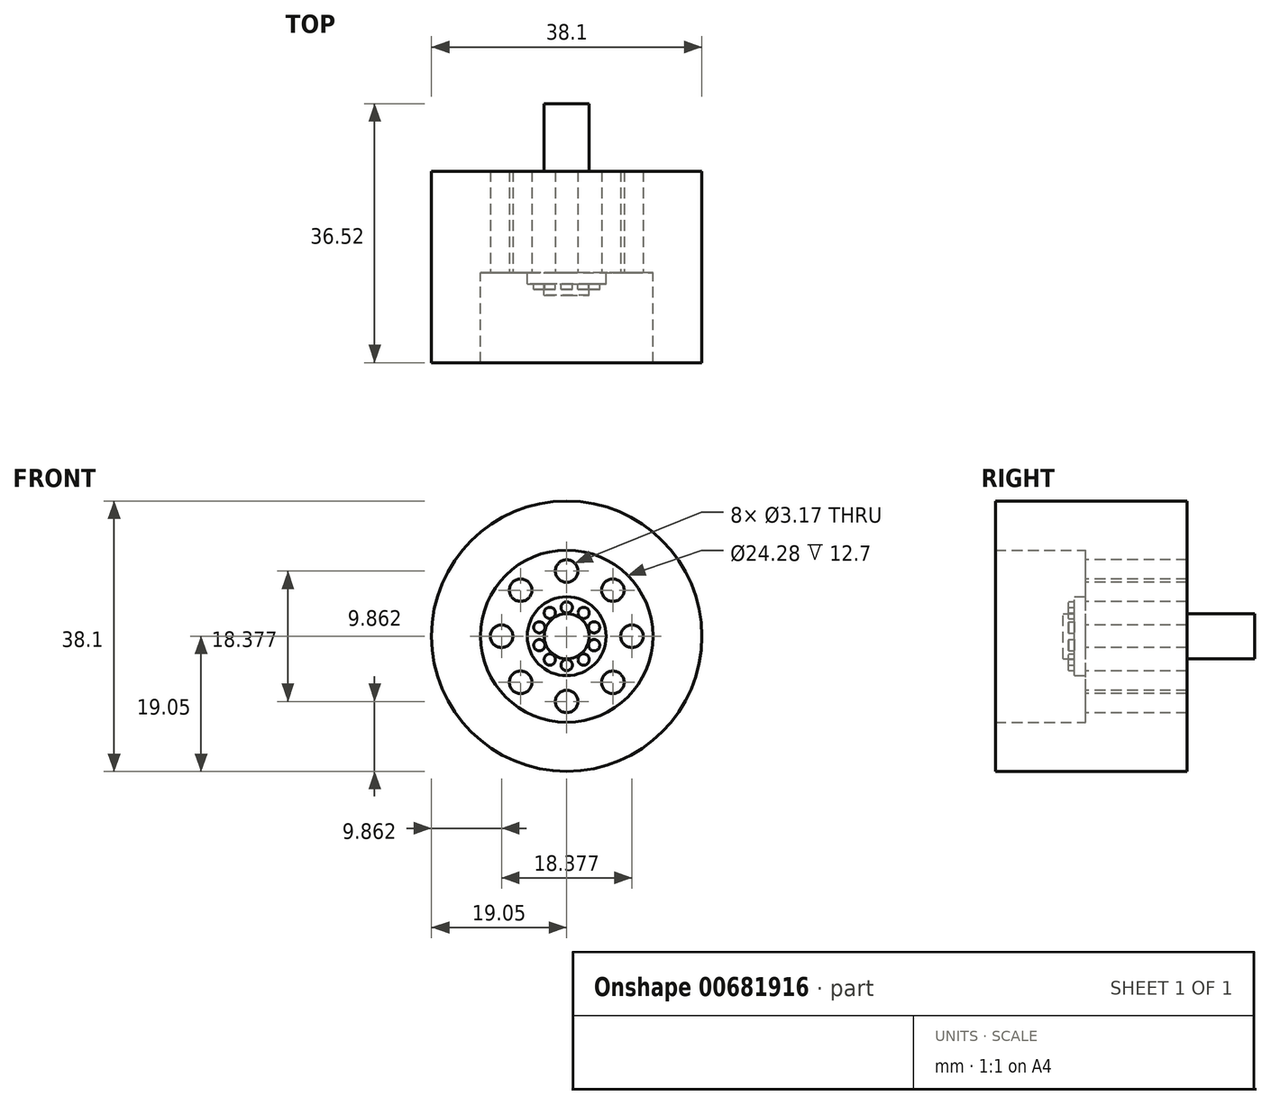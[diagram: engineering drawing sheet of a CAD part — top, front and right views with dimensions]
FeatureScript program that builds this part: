
annotation { "Feature Type Name" : "Feature", "Feature Type Description" : "" }
export const myFeature = defineFeature(function(context is Context, id is Id, definition is map)
    precondition{}
    {
        {
            var Q0;
            Q0=qCreatedBy(makeId("Front.planeOp"),FACE);
            var sketch = newSketch(context, id + "F0", { "sketchPlane" : qUnion([Q0])});
            skCircle(sketch, "E0", {"center": v(0, 0) * mm, "radius": 19.05 * mm});
            skSolve(sketch);
        }
        {
            var Q0;
            Q0=qSketchRegion(id+"F0",true);
            extrude(context, id + "F1", {"entities" : qUnion([Q0]), "depth" : 14.29 * mm, "offsetDistance" : 25.4 * mm});
        }
        {
            var Q0;
            Q0=makeQuery(id+"F1.opExtrude","CAP_FACE",FACE,{"disambiguationData":[OSD([sQuery(id+"F0.wireOp",EDGE,"E0")])],"isStart":false});
            var sketch = newSketch(context, id + "F2", { "sketchPlane" : qUnion([Q0])});
            skCircle(sketch, "E1", {"center": v(0, 9.19) * mm, "radius": 1.59 * mm});
            skCircle(sketch, "E2.1.0", {"center": v(-6.5, 6.5) * mm, "radius": 1.59 * mm});
            skCircle(sketch, "E2.2.0", {"center": v(-9.19, 0) * mm, "radius": 1.59 * mm});
            skCircle(sketch, "E2.3.0", {"center": v(-6.5, -6.5) * mm, "radius": 1.59 * mm});
            skCircle(sketch, "E2.4.0", {"center": v(0, -9.19) * mm, "radius": 1.59 * mm});
            skCircle(sketch, "E2.5.0", {"center": v(6.5, -6.5) * mm, "radius": 1.59 * mm});
            skCircle(sketch, "E2.6.0", {"center": v(9.19, 0) * mm, "radius": 1.59 * mm});
            skCircle(sketch, "E2.7.0", {"center": v(6.5, 6.5) * mm, "radius": 1.59 * mm});
            skPoint(sketch, "E2.center", {"position": v(0, 0) * mm});
            skSolve(sketch);
        }
        {
            var Q0;
            Q0=makeQuery(id+"F2.imprint","IMPRINT",FACE,{"disambiguationData":[TD([[makeQuery(id+"F2.imprint","IMPRINT",EDGE,{"derivedFrom":sQuery(id+"F2.wireOp",EDGE,"E1")}),1.0]])]});
            var Q1;
            Q1=makeQuery(id+"F2.imprint","IMPRINT",FACE,{"disambiguationData":[TD([[makeQuery(id+"F2.imprint","IMPRINT",EDGE,{"derivedFrom":sQuery(id+"F2.wireOp",EDGE,"E2.7.0")}),1.0]])]});
            var Q2;
            Q2=makeQuery(id+"F2.imprint","IMPRINT",FACE,{"disambiguationData":[TD([[makeQuery(id+"F2.imprint","IMPRINT",EDGE,{"derivedFrom":sQuery(id+"F2.wireOp",EDGE,"E2.6.0")}),1.0]])]});
            var Q3;
            Q3=makeQuery(id+"F2.imprint","IMPRINT",FACE,{"disambiguationData":[TD([[makeQuery(id+"F2.imprint","IMPRINT",EDGE,{"derivedFrom":sQuery(id+"F2.wireOp",EDGE,"E2.5.0")}),1.0]])]});
            var Q4;
            Q4=makeQuery(id+"F2.imprint","IMPRINT",FACE,{"disambiguationData":[TD([[makeQuery(id+"F2.imprint","IMPRINT",EDGE,{"derivedFrom":sQuery(id+"F2.wireOp",EDGE,"E2.4.0")}),1.0]])]});
            var Q5;
            Q5=makeQuery(id+"F2.imprint","IMPRINT",FACE,{"disambiguationData":[TD([[makeQuery(id+"F2.imprint","IMPRINT",EDGE,{"derivedFrom":sQuery(id+"F2.wireOp",EDGE,"E2.3.0")}),1.0]])]});
            var Q6;
            Q6=makeQuery(id+"F2.imprint","IMPRINT",FACE,{"disambiguationData":[TD([[makeQuery(id+"F2.imprint","IMPRINT",EDGE,{"derivedFrom":sQuery(id+"F2.wireOp",EDGE,"E2.2.0")}),1.0]])]});
            var Q7;
            Q7=makeQuery(id+"F2.imprint","IMPRINT",FACE,{"disambiguationData":[TD([[makeQuery(id+"F2.imprint","IMPRINT",EDGE,{"derivedFrom":sQuery(id+"F2.wireOp",EDGE,"E2.1.0")}),1.0]])]});
            extrude(context, id + "F3", {"entities" : qUnion([Q0, Q1, Q2, Q3, Q4, Q5, Q6, Q7]), "operationType" : NewBodyOperationType.REMOVE, "oppositeDirection" : true, "depth" : 20.32 * mm, "offsetDistance" : 25.4 * mm});
        }
        {
            var Q0;
            Q0=makeQuery(id+"F1.opExtrude","CAP_FACE",FACE,{"disambiguationData":[OSD([sQuery(id+"F0.wireOp",EDGE,"E0")])],"isStart":false});
            var sketch = newSketch(context, id + "F4", { "sketchPlane" : qUnion([Q0])});
            skCircle(sketch, "E3", {"center": v(0, 0) * mm, "radius": 5.56 * mm});
            skSolve(sketch);
        }
        {
            var Q0;
            Q0=makeQuery(id+"F4.imprint","IMPRINT",FACE,{"disambiguationData":[TD([[makeQuery(id+"F4.imprint","IMPRINT",EDGE,{"derivedFrom":sQuery(id+"F4.wireOp",EDGE,"E3")}),1.0]])]});
            var sketch = newSketch(context, id + "F5", { "sketchPlane" : qUnion([Q0])});
            skCircle(sketch, "E4", {"center": v(0, 0) * mm, "radius": 3.17 * mm});
            skSolve(sketch);
        }
        {
            var Q0;
            Q0=makeQuery(id+"F5.imprint","IMPRINT",FACE,{"disambiguationData":[TD([[makeQuery(id+"F5.imprint","IMPRINT",EDGE,{"derivedFrom":sQuery(id+"F5.wireOp",EDGE,"E4")}),1.0]])]});
            extrude(context, id + "F6", {"entities" : qUnion([Q0]), "operationType" : NewBodyOperationType.ADD, "depth" : 3.17 * mm, "offsetDistance" : 25.4 * mm});
        }
        {
            var Q0;
            Q0=makeQuery(id+"F4.imprint","IMPRINT",FACE,{"disambiguationData":[TD([[makeQuery(id+"F4.imprint","IMPRINT",EDGE,{"derivedFrom":sQuery(id+"F4.wireOp",EDGE,"E3")}),1.0]])]});
            extrude(context, id + "F7", {"entities" : qUnion([Q0]), "operationType" : NewBodyOperationType.ADD, "depth" : 1.59 * mm, "offsetDistance" : 25.4 * mm});
        }
        {
            var Q0;
            Q0=makeQuery(id+"F7.opExtrude","CAP_FACE",FACE,{"disambiguationData":[OSD([sQuery(id+"F4.wireOp",EDGE,"E3")])],"isStart":false});
            var sketch = newSketch(context, id + "F8", { "sketchPlane" : qUnion([Q0])});
            skCircle(sketch, "E5", {"center": v(0, 4.06) * mm, "radius": 0.8 * mm});
            skCircle(sketch, "E6.1.0", {"center": v(-2.39, 3.29) * mm, "radius": 0.8 * mm});
            skCircle(sketch, "E6.2.0", {"center": v(-3.86, 1.26) * mm, "radius": 0.8 * mm});
            skCircle(sketch, "E6.3.0", {"center": v(-3.86, -1.26) * mm, "radius": 0.8 * mm});
            skCircle(sketch, "E6.4.0", {"center": v(-2.39, -3.29) * mm, "radius": 0.8 * mm});
            skCircle(sketch, "E6.5.0", {"center": v(0, -4.06) * mm, "radius": 0.8 * mm});
            skCircle(sketch, "E6.6.0", {"center": v(2.39, -3.29) * mm, "radius": 0.8 * mm});
            skCircle(sketch, "E6.7.0", {"center": v(3.86, -1.26) * mm, "radius": 0.8 * mm});
            skCircle(sketch, "E6.8.0", {"center": v(3.86, 1.26) * mm, "radius": 0.8 * mm});
            skCircle(sketch, "E6.9.0", {"center": v(2.39, 3.29) * mm, "radius": 0.8 * mm});
            skPoint(sketch, "E6.center", {"position": v(0, 0) * mm});
            skSolve(sketch);
        }
        {
            var Q0;
            Q0=makeQuery(id+"F8.imprint","IMPRINT",FACE,{"disambiguationData":[TD([[makeQuery(id+"F8.imprint","IMPRINT",EDGE,{"derivedFrom":sQuery(id+"F8.wireOp",EDGE,"E5")}),1.0]])]});
            var Q1;
            Q1=makeQuery(id+"F8.imprint","IMPRINT",FACE,{"disambiguationData":[TD([[makeQuery(id+"F8.imprint","IMPRINT",EDGE,{"derivedFrom":sQuery(id+"F8.wireOp",EDGE,"E6.9.0")}),1.0]])]});
            var Q2;
            Q2=makeQuery(id+"F8.imprint","IMPRINT",FACE,{"disambiguationData":[TD([[makeQuery(id+"F8.imprint","IMPRINT",EDGE,{"derivedFrom":sQuery(id+"F8.wireOp",EDGE,"E6.8.0")}),1.0]])]});
            var Q3;
            Q3=makeQuery(id+"F8.imprint","IMPRINT",FACE,{"disambiguationData":[TD([[makeQuery(id+"F8.imprint","IMPRINT",EDGE,{"derivedFrom":sQuery(id+"F8.wireOp",EDGE,"E6.7.0")}),1.0]])]});
            var Q4;
            Q4=makeQuery(id+"F8.imprint","IMPRINT",FACE,{"disambiguationData":[TD([[makeQuery(id+"F8.imprint","IMPRINT",EDGE,{"derivedFrom":sQuery(id+"F8.wireOp",EDGE,"E6.6.0")}),1.0]])]});
            var Q5;
            Q5=makeQuery(id+"F8.imprint","IMPRINT",FACE,{"disambiguationData":[TD([[makeQuery(id+"F8.imprint","IMPRINT",EDGE,{"derivedFrom":sQuery(id+"F8.wireOp",EDGE,"E6.5.0")}),1.0]])]});
            var Q6;
            Q6=makeQuery(id+"F8.imprint","IMPRINT",FACE,{"disambiguationData":[TD([[makeQuery(id+"F8.imprint","IMPRINT",EDGE,{"derivedFrom":sQuery(id+"F8.wireOp",EDGE,"E6.4.0")}),1.0]])]});
            var Q7;
            Q7=makeQuery(id+"F8.imprint","IMPRINT",FACE,{"disambiguationData":[TD([[makeQuery(id+"F8.imprint","IMPRINT",EDGE,{"derivedFrom":sQuery(id+"F8.wireOp",EDGE,"E6.3.0")}),1.0]])]});
            var Q8;
            Q8=makeQuery(id+"F8.imprint","IMPRINT",FACE,{"disambiguationData":[TD([[makeQuery(id+"F8.imprint","IMPRINT",EDGE,{"derivedFrom":sQuery(id+"F8.wireOp",EDGE,"E6.2.0")}),1.0]])]});
            var Q9;
            Q9=makeQuery(id+"F8.imprint","IMPRINT",FACE,{"disambiguationData":[TD([[makeQuery(id+"F8.imprint","IMPRINT",EDGE,{"derivedFrom":sQuery(id+"F8.wireOp",EDGE,"E6.1.0")}),1.0]])]});
            extrude(context, id + "F9", {"entities" : qUnion([Q0, Q1, Q2, Q3, Q4, Q5, Q6, Q7, Q8, Q9]), "depth" : 0.8 * mm, "offsetDistance" : 25.4 * mm});
        }
        {
            var Q0;
            Q0=makeQuery(id+"F1.opExtrude","CAP_FACE",FACE,{"disambiguationData":[OSD([sQuery(id+"F0.wireOp",EDGE,"E0")])],"isStart":true});
            var sketch = newSketch(context, id + "F10", { "sketchPlane" : qUnion([Q0])});
            skCircle(sketch, "E7", {"center": v(0, 0) * mm, "radius": 3.18 * mm});
            skSolve(sketch);
        }
        {
            var Q0;
            Q0=makeQuery(id+"F10.imprint","IMPRINT",FACE,{"disambiguationData":[TD([[makeQuery(id+"F10.imprint","IMPRINT",EDGE,{"derivedFrom":sQuery(id+"F10.wireOp",EDGE,"E7")}),1.0]])]});
            extrude(context, id + "F11", {"entities" : qUnion([Q0]), "operationType" : NewBodyOperationType.ADD, "depth" : 9.52 * mm, "offsetDistance" : 25.4 * mm});
        }
        {
            var Q0;
            Q0=makeQuery(id+"F1.opExtrude","CAP_FACE",FACE,{"disambiguationData":[OSD([sQuery(id+"F0.wireOp",EDGE,"E0")])],"isStart":false});
            var sketch = newSketch(context, id + "F12", { "sketchPlane" : qUnion([Q0])});
            skCircle(sketch, "E8", {"center": v(0, 0) * mm, "radius": 12.14 * mm});
            skSolve(sketch);
        }
        {
            var Q0;
            Q0=makeQuery(id+"F12.imprint","IMPRINT",FACE,{"disambiguationData":[TD([[makeQuery(id+"F12.imprint","IMPRINT",EDGE,{"derivedFrom":sQuery(id+"F12.wireOp",EDGE,"E8")}),-1.0]])]});
            extrude(context, id + "F13", {"entities" : qUnion([Q0]), "operationType" : NewBodyOperationType.ADD, "depth" : 12.7 * mm, "offsetDistance" : 25.4 * mm});
        }
    });
